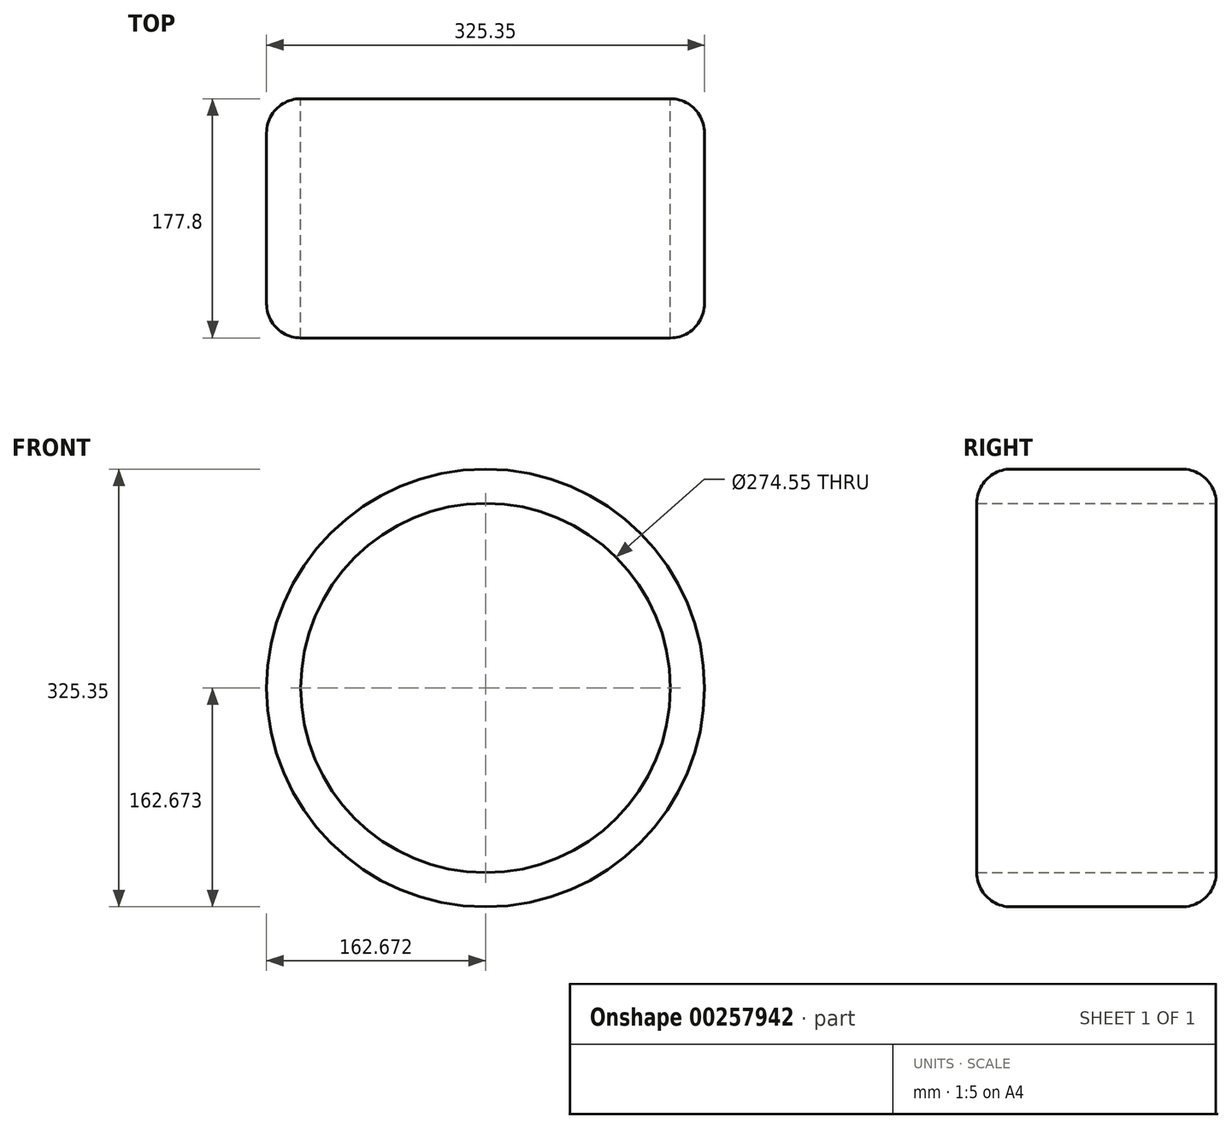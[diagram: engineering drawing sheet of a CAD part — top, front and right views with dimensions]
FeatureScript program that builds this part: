
annotation { "Feature Type Name" : "Feature", "Feature Type Description" : "" }
export const myFeature = defineFeature(function(context is Context, id is Id, definition is map)
    precondition{}
    {
        {
            var Q0;
            Q0=qCreatedBy(makeId("Front.planeOp"),FACE);
            var sketch = newSketch(context, id + "F0", { "sketchPlane" : qUnion([Q0])});
            skCircle(sketch, "E0", {"center": v(-6.23, -7.79) * mm, "radius": 137.27 * mm});
            skSolve(sketch);
        }
        {
            var Q0;
            Q0=makeQuery(id+"F0.imprint","IMPRINT",FACE,{"disambiguationData":[TD([[makeQuery(id+"F0.imprint","IMPRINT",EDGE,{"derivedFrom":sQuery(id+"F0.wireOp",EDGE,"E0")}),1.0]])]});
            extrude(context, id + "F1", {"entities" : qUnion([Q0]), "depth" : 177.8 * mm});
        }
        {
            var Q0;
            Q0=makeQuery(id+"F1.opExtrude","CAP_FACE",FACE,{"disambiguationData":[OSD([sQuery(id+"F0.wireOp",EDGE,"E0")])],"isStart":false});
            var Q1;
            Q1=makeQuery(id+"F1.opExtrude","CAP_FACE",FACE,{"disambiguationData":[OSD([sQuery(id+"F0.wireOp",EDGE,"E0")])],"isStart":true});
            shell(context, id + "F2", {"entities" : qUnion([Q0, Q1]), "thickness" : 25.4 * mm, "oppositeDirection" : true});
        }
        {
            var Q0;
            Q0=makeQuery(id+"F1.opExtrude","CAP_EDGE",EDGE,{"disambiguationData":[OSD([sQuery(id+"F0.wireOp",EDGE,"E0")])],"isStart":false});
            var Q1;
            Q1=makeQuery(id+"F1.opExtrude","CAP_EDGE",EDGE,{"disambiguationData":[OSD([sQuery(id+"F0.wireOp",EDGE,"E0")])],"isStart":true});
            fillet(context, id + "F3", {"entities" : qUnion([Q0, Q1]), "radius" : 25.4 * mm, "tangentPropagation" : true, "allowEdgeOverflow" : false});
        }
    });
